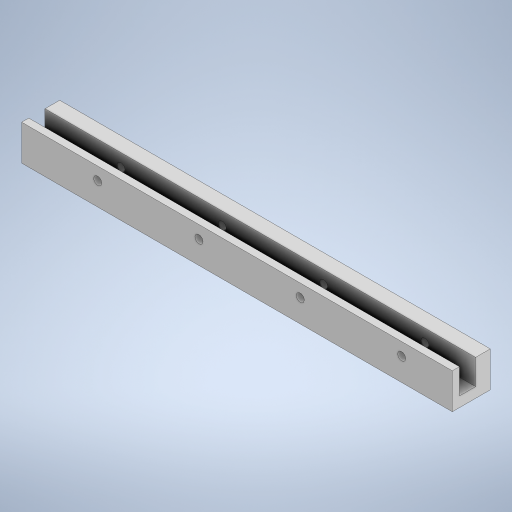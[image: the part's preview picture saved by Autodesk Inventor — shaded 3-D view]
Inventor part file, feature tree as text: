
AUTODESK INVENTOR PART (.ipt)
format: ipt  version: 2023 (Build 270158000, 158)  size: 323,584 bytes
history: native  units: mm
features: sketch x10, extrude x7, hole x3, other x1
ambient origin geometry x8: Origin, YZ Plane, XZ Plane, XY Plane, X Axis, Y Axis, Z Axis, Center Point
bodies: Body1 (feature_tree)
feature tree (21):
  other  "ソリッド1"
  extrude  "押し出し1"  Depth=180.0mm
  extrude  "押し出し2"  Depth=6.0mm
  extrude  "押し出し3"  Depth=17.0mm TaperAngle=0.0deg
  extrude  "押し出し4"  Depth=170.0mm
  extrude  "押し出し5"  Depth=6.0mm
  hole  "穴1"  [1 undecoded]
  hole  "穴2"  [1 undecoded]
  extrude  "押し出し6"  Depth=14.0mm TaperAngle=0.0deg
  hole  "穴3"  [1 undecoded]
  extrude  "押し出し7"  Depth=13.0mm TaperAngle=0.0deg
  sketch  "スケッチ1"
  sketch  "スケッチ2"
  sketch  "スケッチ3"
  sketch  "スケッチ4"
  sketch  "スケッチ5"
  sketch  "スケッチ6"
  sketch  "スケッチ7"
  sketch  "スケッチ8"
  sketch  "スケッチ10"
  sketch  "スケッチ11"
note: 3 required parameter values undecoded (feature->parameter linkage not recoverable at this tier; creation-order binding heuristic only, values carry confidence <= 0.55)
